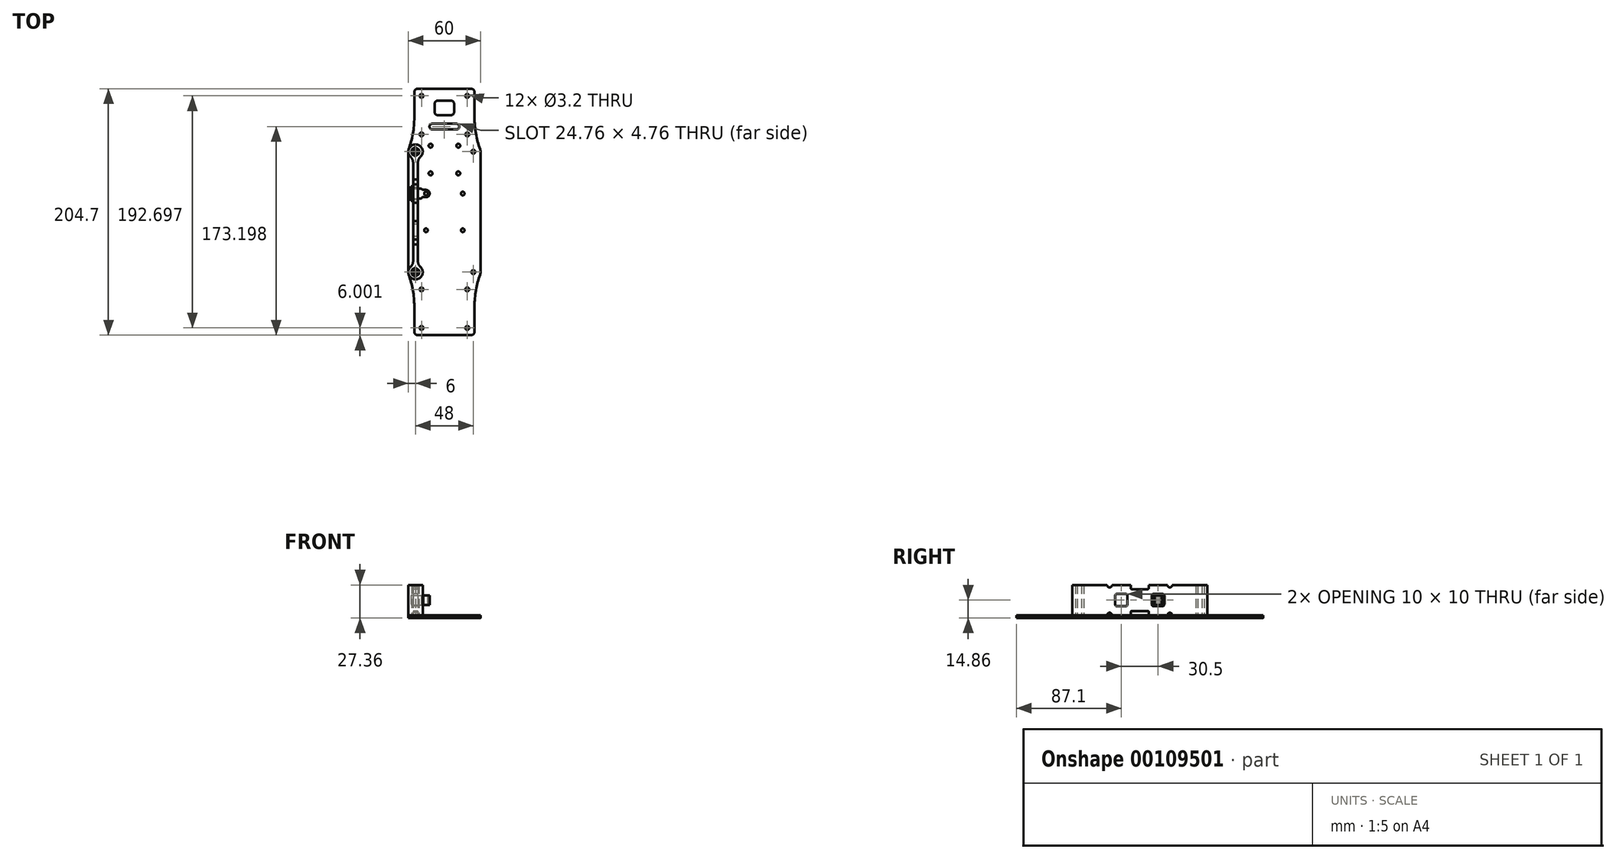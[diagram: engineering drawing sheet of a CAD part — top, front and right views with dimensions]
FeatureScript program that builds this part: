
annotation { "Feature Type Name" : "Feature", "Feature Type Description" : "" }
export const myFeature = defineFeature(function(context is Context, id is Id, definition is map)
    precondition{}
    {
        {
            var Q0;
            Q0=qCreatedBy(makeId("Top.planeOp"),FACE);
            var sketch = newSketch(context, id + "F0", { "sketchPlane" : qUnion([Q0])});
            skLineSegment(sketch, "E0", {"start": v(0, 102.35) * mm, "end": v(-22, 102.35) * mm});
            skLineSegment(sketch, "E1", {"start": v(-25, 99.35) * mm, "end": v(-25, 78.35) * mm});
            skLineSegment(sketch, "E2", {"start": v(-22, -102.35) * mm, "end": v(0, -102.35) * mm});
            skArc(sketch, "E3.filletArc", {"start": v(-22, 102.35) * mm, "mid": v(-24.12, 101.47) * mm, "end": v(-25, 99.35) * mm});
            skArc(sketch, "E4.filletArc", {"start": v(-25, -99.35) * mm, "mid": v(-24.12, -101.47) * mm, "end": v(-22, -102.35) * mm});
            skArc(sketch, "E5.filletArc", {"start": v(-29.64, 52.05) * mm, "mid": v(-29.9, 51.04) * mm, "end": v(-30, 50) * mm});
            skArc(sketch, "E6.MirrorCS", {"start": v(-29.64, -52.05) * mm, "mid": v(-29.9, -51.04) * mm, "end": v(-30, -50) * mm});
            skLineSegment(sketch, "E7.trimOffspring", {"start": v(-25, -78.35) * mm, "end": v(-25, -99.35) * mm});
            skArc(sketch, "E8", {"start": v(-25, -78.35) * mm, "mid": v(-26.17, -65) * mm, "end": v(-29.64, -52.05) * mm});
            skArc(sketch, "E9", {"start": v(-29.64, 52.05) * mm, "mid": v(-26.17, 65) * mm, "end": v(-25, 78.35) * mm});
            skCircle(sketch, "E10", {"center": v(0, 0) * mm, "radius": 125 * mm, "construction": true});
            skLineSegment(sketch, "E11", {"start": v(-95.76, 80.35) * mm, "end": v(95.76, -80.35) * mm, "construction": true});
            skLineSegment(sketch, "E12", {"start": v(95.76, 80.35) * mm, "end": v(-95.76, -80.35) * mm, "construction": true});
            skLineSegment(sketch, "E13", {"start": v(0, 125) * mm, "end": v(0, -125) * mm, "construction": true});
            skLineSegment(sketch, "E14", {"start": v(-95.76, 80.35) * mm, "end": v(95.76, 80.35) * mm, "construction": true});
            skLineSegment(sketch, "E15", {"start": v(-95.76, -80.35) * mm, "end": v(95.76, -80.35) * mm, "construction": true});
            skLineSegment(sketch, "E16", {"start": v(-30, 50) * mm, "end": v(-30, -50) * mm});
            skLineSegment(sketch, "E17.MirrorCS", {"start": v(0, 102.35) * mm, "end": v(22, 102.35) * mm});
            skArc(sketch, "E18.MirrorCS", {"start": v(22, 102.35) * mm, "mid": v(24.12, 101.47) * mm, "end": v(25, 99.35) * mm});
            skLineSegment(sketch, "E19.MirrorCS", {"start": v(25, 99.35) * mm, "end": v(25, 78.35) * mm});
            skArc(sketch, "E20.MirrorCS", {"start": v(29.64, 52.05) * mm, "mid": v(26.17, 65) * mm, "end": v(25, 78.35) * mm});
            skArc(sketch, "E21.MirrorCS", {"start": v(29.64, 52.05) * mm, "mid": v(29.9, 51.04) * mm, "end": v(30, 50) * mm});
            skLineSegment(sketch, "E22.MirrorCS", {"start": v(30, 50) * mm, "end": v(30, -50) * mm});
            skArc(sketch, "E23.MirrorCS", {"start": v(29.64, -52.05) * mm, "mid": v(29.9, -51.04) * mm, "end": v(30, -50) * mm});
            skArc(sketch, "E24.MirrorCS", {"start": v(25, -78.35) * mm, "mid": v(26.17, -65) * mm, "end": v(29.64, -52.05) * mm});
            skArc(sketch, "E25.MirrorCS", {"start": v(25, -99.35) * mm, "mid": v(24.12, -101.47) * mm, "end": v(22, -102.35) * mm});
            skLineSegment(sketch, "E26.MirrorCS", {"start": v(22, -102.35) * mm, "end": v(0, -102.35) * mm});
            skLineSegment(sketch, "E27.MirrorCS", {"start": v(25, -78.35) * mm, "end": v(25, -99.35) * mm});
            skSolve(sketch);
        }
        {
            var Q0;
            Q0=qSketchRegion(id+"F0",true);
            extrude(context, id + "F1", {"entities" : qUnion([Q0]), "oppositeDirection" : true, "depth" : 2.36 * mm});
        }
        {
            var Q0;
            Q0=makeQuery(id+"F1.opExtrude","CAP_FACE",FACE,{"disambiguationData":[OSD([sQuery(id+"F0.wireOp",EDGE,"E0"),sQuery(id+"F0.wireOp",EDGE,"E1"),sQuery(id+"F0.wireOp",EDGE,"E2"),sQuery(id+"F0.wireOp",EDGE,"E3.filletArc"),sQuery(id+"F0.wireOp",EDGE,"E4.filletArc"),sQuery(id+"F0.wireOp",EDGE,"d22b67ea-32aa-4b1a-bfbd-94ae52c1f5b30.MirrorCS"),sQuery(id+"F0.wireOp",EDGE,"d22b67ea-32aa-4b1a-bfbd-94ae52c1f5b31.MirrorCS"),sQuery(id+"F0.wireOp",EDGE,"d22b67ea-32aa-4b1a-bfbd-94ae52c1f5b32.MirrorCS"),sQuery(id+"F0.wireOp",EDGE,"d22b67ea-32aa-4b1a-bfbd-94ae52c1f5b33.MirrorCS"),sQuery(id+"F0.wireOp",EDGE,"d22b67ea-32aa-4b1a-bfbd-94ae52c1f5b34.MirrorCS")])],"isStart":true});
            var sketch = newSketch(context, id + "F2", { "sketchPlane" : qUnion([Q0])});
            skCircle(sketch, "E28", {"center": v(-19, 96.35) * mm, "radius": 1.6 * mm});
            skCircle(sketch, "E29", {"center": v(-19, 64.35) * mm, "radius": 1.6 * mm});
            skCircle(sketch, "E30", {"center": v(-19, -96.35) * mm, "radius": 1.6 * mm});
            skCircle(sketch, "E31", {"center": v(-19, -64.35) * mm, "radius": 1.6 * mm});
            skCircle(sketch, "E32", {"center": v(-24, -50) * mm, "radius": 1.6 * mm});
            skCircle(sketch, "E33", {"center": v(-24, 50) * mm, "radius": 1.6 * mm});
            skLineSegment(sketch, "E34", {"start": v(-19, 96.35) * mm, "end": v(-19, -96.35) * mm, "construction": true});
            skCircle(sketch, "E35.MirrorC", {"center": v(19, 96.35) * mm, "radius": 1.6 * mm});
            skCircle(sketch, "E36.MirrorC", {"center": v(19, 64.35) * mm, "radius": 1.6 * mm});
            skCircle(sketch, "E37.MirrorC", {"center": v(24, 50) * mm, "radius": 1.6 * mm});
            skCircle(sketch, "E38.MirrorC", {"center": v(24, -50) * mm, "radius": 1.6 * mm});
            skCircle(sketch, "E39.MirrorC", {"center": v(19, -64.35) * mm, "radius": 1.6 * mm});
            skCircle(sketch, "E40.MirrorC", {"center": v(19, -96.35) * mm, "radius": 1.6 * mm});
            skLineSegment(sketch, "E41", {"start": v(-15.25, 15.25) * mm, "end": v(-15.25, -15.25) * mm, "construction": true});
            skPoint(sketch, "E42", {"position": v(-15.25, 0) * mm});
            skLineSegment(sketch, "E43", {"start": v(0, 0) * mm, "end": v(-30, 0) * mm, "construction": true});
            skCircle(sketch, "E44", {"center": v(-15.25, -15.25) * mm, "radius": 1.5 * mm});
            skCircle(sketch, "E45", {"center": v(-15.25, 15.25) * mm, "radius": 1.5 * mm});
            skCircle(sketch, "E46.MirrorC", {"center": v(15.25, 15.25) * mm, "radius": 1.5 * mm});
            skCircle(sketch, "E47.MirrorC", {"center": v(15.25, -15.25) * mm, "radius": 1.5 * mm});
            skSolve(sketch);
        }
        {
            var Q0;
            Q0=qSketchRegion(id+"F2",true);
            extrude(context, id + "F3", {"entities" : qUnion([Q0]), "operationType" : NewBodyOperationType.REMOVE, "endBound" : BoundingType.THROUGH_ALL, "oppositeDirection" : true, "depth" : 25.4 * mm});
        }
        {
            var Q0;
            Q0=qCreatedBy(makeId("Top.planeOp"),FACE);
            var sketch = newSketch(context, id + "F4", { "sketchPlane" : qUnion([Q0])});
            skCircle(sketch, "E48.cCircle", {"center": v(-24, 50) * mm, "radius": 3.1 * mm, "construction": true});
            skLineSegment(sketch, "E48.0", {"start": v(-24, 53.58) * mm, "end": v(-20.9, 51.79) * mm, "construction": true});
            skLineSegment(sketch, "E48.1", {"start": v(-20.9, 51.79) * mm, "end": v(-20.9, 48.21) * mm, "construction": true});
            skLineSegment(sketch, "E48.2", {"start": v(-20.9, 48.21) * mm, "end": v(-24, 46.42) * mm, "construction": true});
            skLineSegment(sketch, "E48.3", {"start": v(-24, 46.42) * mm, "end": v(-27.1, 48.21) * mm, "construction": true});
            skLineSegment(sketch, "E48.4", {"start": v(-27.1, 48.21) * mm, "end": v(-27.1, 51.79) * mm, "construction": true});
            skLineSegment(sketch, "E48.5", {"start": v(-27.1, 51.79) * mm, "end": v(-24, 53.58) * mm, "construction": true});
            skPoint(sketch, "E48.0.midPoint", {"position": v(-22.45, 52.68) * mm});
            skArc(sketch, "E49", {"start": v(-20, 45.53) * mm, "mid": v(-24, 56) * mm, "end": v(-28, 45.53) * mm});
            skArc(sketch, "E50", {"start": v(-28, -45.53) * mm, "mid": v(-24, -56) * mm, "end": v(-20, -45.53) * mm});
            skLineSegment(sketch, "E51", {"start": v(-26, 41.06) * mm, "end": v(-26, -41.06) * mm});
            skLineSegment(sketch, "E52", {"start": v(-22, 41.06) * mm, "end": v(-22, -41.06) * mm});
            skPoint(sketch, "E53.visualSharp", {"position": v(-26, 44.34) * mm});
            skArc(sketch, "E53.filletArc", {"start": v(-26, 41.06) * mm, "mid": v(-26.52, 43.5) * mm, "end": v(-28, 45.53) * mm});
            skPoint(sketch, "E54.visualSharp", {"position": v(-22, 44.34) * mm});
            skArc(sketch, "E54.filletArc", {"start": v(-20, 45.53) * mm, "mid": v(-21.48, 43.5) * mm, "end": v(-22, 41.06) * mm});
            skPoint(sketch, "E55.visualSharp", {"position": v(-22, -44.34) * mm});
            skArc(sketch, "E55.filletArc", {"start": v(-22, -41.06) * mm, "mid": v(-21.48, -43.5) * mm, "end": v(-20, -45.53) * mm});
            skPoint(sketch, "E56.visualSharp", {"position": v(-26, -44.34) * mm});
            skArc(sketch, "E56.filletArc", {"start": v(-28, -45.53) * mm, "mid": v(-26.52, -43.5) * mm, "end": v(-26, -41.06) * mm});
            skLineSegment(sketch, "E57", {"start": v(-24, 50) * mm, "end": v(-24, -50) * mm, "construction": true});
            skSolve(sketch);
        }
        {
            var Q0;
            Q0=qSketchRegion(id+"F4",true);
            extrude(context, id + "F5", {"entities" : qUnion([Q0]), "depth" : 25 * mm});
        }
        {
            var Q0;
            Q0=makeQuery(id+"F5.opExtrude","CAP_FACE",FACE,{"disambiguationData":[OSD([sQuery(id+"F4.wireOp",EDGE,"E49"),sQuery(id+"F4.wireOp",EDGE,"E50"),sQuery(id+"F4.wireOp",EDGE,"E51"),sQuery(id+"F4.wireOp",EDGE,"E52"),sQuery(id+"F4.wireOp",EDGE,"E53.filletArc"),sQuery(id+"F4.wireOp",EDGE,"E54.filletArc"),sQuery(id+"F4.wireOp",EDGE,"E55.filletArc"),sQuery(id+"F4.wireOp",EDGE,"E56.filletArc")])],"isStart":true});
            var sketch = newSketch(context, id + "F6", { "sketchPlane" : qUnion([Q0])});
            skCircle(sketch, "E58.cCircle", {"center": v(-24, -50) * mm, "radius": 3.05 * mm, "construction": true});
            skLineSegment(sketch, "E58.0", {"start": v(-27.05, -48.24) * mm, "end": v(-24, -46.48) * mm});
            skLineSegment(sketch, "E58.1", {"start": v(-24, -46.48) * mm, "end": v(-20.95, -48.24) * mm});
            skLineSegment(sketch, "E58.2", {"start": v(-20.95, -48.24) * mm, "end": v(-20.95, -51.76) * mm});
            skLineSegment(sketch, "E58.3", {"start": v(-20.95, -51.76) * mm, "end": v(-24, -53.52) * mm});
            skLineSegment(sketch, "E58.4", {"start": v(-24, -53.52) * mm, "end": v(-27.05, -51.76) * mm});
            skLineSegment(sketch, "E58.5", {"start": v(-27.05, -51.76) * mm, "end": v(-27.05, -48.24) * mm});
            skPoint(sketch, "E58.0.midPoint", {"position": v(-25.53, -47.36) * mm});
            skCircle(sketch, "E59.cCircle", {"center": v(-24, 50) * mm, "radius": 3.05 * mm, "construction": true});
            skLineSegment(sketch, "E59.0", {"start": v(-27.05, 51.76) * mm, "end": v(-24, 53.52) * mm});
            skLineSegment(sketch, "E59.1", {"start": v(-24, 53.52) * mm, "end": v(-20.95, 51.76) * mm});
            skLineSegment(sketch, "E59.2", {"start": v(-20.95, 51.76) * mm, "end": v(-20.95, 48.24) * mm});
            skLineSegment(sketch, "E59.3", {"start": v(-20.95, 48.24) * mm, "end": v(-24, 46.48) * mm});
            skLineSegment(sketch, "E59.4", {"start": v(-24, 46.48) * mm, "end": v(-27.05, 48.24) * mm});
            skLineSegment(sketch, "E59.5", {"start": v(-27.05, 48.24) * mm, "end": v(-27.05, 51.76) * mm});
            skPoint(sketch, "E59.0.midPoint", {"position": v(-25.52, 52.64) * mm});
            skSolve(sketch);
        }
        {
            var Q0;
            Q0=qSketchRegion(id+"F6",true);
            var Q1;
            Q1=makeQuery(id+"F5.opExtrude","CAP_FACE",FACE,{"disambiguationData":[OSD([sQuery(id+"F4.wireOp",EDGE,"E49"),sQuery(id+"F4.wireOp",EDGE,"E50"),sQuery(id+"F4.wireOp",EDGE,"E51"),sQuery(id+"F4.wireOp",EDGE,"E52"),sQuery(id+"F4.wireOp",EDGE,"E53.filletArc"),sQuery(id+"F4.wireOp",EDGE,"E54.filletArc"),sQuery(id+"F4.wireOp",EDGE,"E55.filletArc"),sQuery(id+"F4.wireOp",EDGE,"E56.filletArc")])],"isStart":false});
            extrude(context, id + "F7", {"entities" : qUnion([Q0]), "operationType" : NewBodyOperationType.REMOVE, "endBound" : BoundingType.UP_TO_SURFACE, "oppositeDirection" : true, "endBoundEntityFace" : qUnion([Q1]), "depth" : 25 * mm});
        }
        {
            var Q0;
            Q0=makeQuery(id+"F5.opExtrude","SWEPT_FACE",FACE,{"disambiguationData":[OSD([sQuery(id+"F4.wireOp",EDGE,"E51")])]});
            var sketch = newSketch(context, id + "F8", { "sketchPlane" : qUnion([Q0])});
            skLineSegment(sketch, "E60", {"start": v(-21.13, 12.5) * mm, "end": v(21.13, 12.5) * mm, "construction": true});
            skLineSegment(sketch, "E61.bottom", {"start": v(-11.25, 17.5) * mm, "end": v(-19.25, 17.5) * mm});
            skLineSegment(sketch, "E61.top", {"start": v(-11.25, 7.5) * mm, "end": v(-19.25, 7.5) * mm});
            skLineSegment(sketch, "E61.left", {"start": v(-10.25, 16.5) * mm, "end": v(-10.25, 8.5) * mm});
            skLineSegment(sketch, "E61.right", {"start": v(-20.25, 16.5) * mm, "end": v(-20.25, 8.5) * mm});
            skPoint(sketch, "E61.middle", {"position": v(-15.25, 12.5) * mm});
            skPoint(sketch, "E62.visualSharp", {"position": v(-20.25, 17.5) * mm});
            skArc(sketch, "E62.filletArc", {"start": v(-19.25, 17.5) * mm, "mid": v(-19.96, 17.2) * mm, "end": v(-20.25, 16.5) * mm});
            skPoint(sketch, "E63.visualSharp", {"position": v(-20.25, 7.5) * mm});
            skArc(sketch, "E63.filletArc", {"start": v(-20.25, 8.5) * mm, "mid": v(-19.96, 7.8) * mm, "end": v(-19.25, 7.5) * mm});
            skPoint(sketch, "E64.visualSharp", {"position": v(-10.25, 7.5) * mm});
            skArc(sketch, "E64.filletArc", {"start": v(-11.25, 7.5) * mm, "mid": v(-10.54, 7.8) * mm, "end": v(-10.25, 8.5) * mm});
            skPoint(sketch, "E65.visualSharp", {"position": v(-10.25, 17.5) * mm});
            skArc(sketch, "E65.filletArc", {"start": v(-10.25, 16.5) * mm, "mid": v(-10.54, 17.2) * mm, "end": v(-11.25, 17.5) * mm});
            skLineSegment(sketch, "E66.bottom", {"start": v(-7.5, 0) * mm, "end": v(7.5, 0) * mm});
            skLineSegment(sketch, "E66.top", {"start": v(-6.5, 3.5) * mm, "end": v(6.5, 3.5) * mm});
            skLineSegment(sketch, "E66.left", {"start": v(-7.5, 0) * mm, "end": v(-7.5, 2.5) * mm});
            skLineSegment(sketch, "E66.right", {"start": v(7.5, 0) * mm, "end": v(7.5, 2.5) * mm});
            skPoint(sketch, "E67.visualSharp", {"position": v(-7.5, 3.5) * mm});
            skArc(sketch, "E67.filletArc", {"start": v(-6.5, 3.5) * mm, "mid": v(-7.2, 3.2) * mm, "end": v(-7.5, 2.5) * mm});
            skPoint(sketch, "E68.visualSharp", {"position": v(7.5, 3.5) * mm});
            skArc(sketch, "E68.filletArc", {"start": v(7.5, 2.5) * mm, "mid": v(7.2, 3.2) * mm, "end": v(6.5, 3.5) * mm});
            skArc(sketch, "E69", {"start": v(-27, 25) * mm, "mid": v(-25, 23) * mm, "end": v(-23, 25) * mm});
            skLineSegment(sketch, "E70", {"start": v(-25, 25) * mm, "end": v(-25, 0) * mm, "construction": true});
            skArc(sketch, "E71", {"start": v(-23, 0) * mm, "mid": v(-25, 2) * mm, "end": v(-27, 0) * mm});
            skLineSegment(sketch, "E72", {"start": v(-27, 25) * mm, "end": v(-23, 25) * mm});
            skLineSegment(sketch, "E73", {"start": v(-27, 0) * mm, "end": v(-23, 0) * mm});
            skLineSegment(sketch, "E74", {"start": v(0, 25) * mm, "end": v(0, 0) * mm, "construction": true});
            skPoint(sketch, "E75", {"position": v(0, 12.5) * mm});
            skArc(sketch, "E76.MirrorCS", {"start": v(11.25, 7.5) * mm, "mid": v(10.54, 7.8) * mm, "end": v(10.25, 8.5) * mm});
            skArc(sketch, "E77.MirrorCS", {"start": v(10.25, 16.5) * mm, "mid": v(10.54, 17.2) * mm, "end": v(11.25, 17.5) * mm});
            skArc(sketch, "E78.MirrorCS", {"start": v(20.25, 8.5) * mm, "mid": v(19.96, 7.8) * mm, "end": v(19.25, 7.5) * mm});
            skArc(sketch, "E79.MirrorCS", {"start": v(19.25, 17.5) * mm, "mid": v(19.96, 17.2) * mm, "end": v(20.25, 16.5) * mm});
            skPoint(sketch, "E80.MirrorP", {"position": v(10.25, 17.5) * mm});
            skLineSegment(sketch, "E81.MirrorCS", {"start": v(20.25, 16.5) * mm, "end": v(20.25, 8.5) * mm});
            skLineSegment(sketch, "E82.MirrorCS", {"start": v(10.25, 16.5) * mm, "end": v(10.25, 8.5) * mm});
            skLineSegment(sketch, "E83.MirrorCS", {"start": v(11.25, 17.5) * mm, "end": v(19.25, 17.5) * mm});
            skLineSegment(sketch, "E84.MirrorCS", {"start": v(11.25, 7.5) * mm, "end": v(19.25, 7.5) * mm});
            skPoint(sketch, "E85.MirrorP", {"position": v(20.25, 7.5) * mm});
            skPoint(sketch, "E86.MirrorP", {"position": v(15.25, 12.5) * mm});
            skPoint(sketch, "E87.MirrorP", {"position": v(20.25, 17.5) * mm});
            skPoint(sketch, "E88.MirrorP", {"position": v(10.25, 7.5) * mm});
            skLineSegment(sketch, "E89.MirrorCS", {"start": v(27, 25) * mm, "end": v(23, 25) * mm});
            skLineSegment(sketch, "E90.MirrorCS", {"start": v(25, 25) * mm, "end": v(25, 0) * mm, "construction": true});
            skArc(sketch, "E91.MirrorCS", {"start": v(27, 25) * mm, "mid": v(25, 23) * mm, "end": v(23, 25) * mm});
            skLineSegment(sketch, "E92.MirrorCS", {"start": v(27, 0) * mm, "end": v(23, 0) * mm});
            skArc(sketch, "E93.MirrorCS", {"start": v(23, 0) * mm, "mid": v(25, 2) * mm, "end": v(27, 0) * mm});
            skArc(sketch, "E94.MirrorCS", {"start": v(-6.5, 21.5) * mm, "mid": v(-7.2, 21.8) * mm, "end": v(-7.5, 22.5) * mm});
            skArc(sketch, "E95.MirrorCS", {"start": v(7.5, 22.5) * mm, "mid": v(7.2, 21.8) * mm, "end": v(6.5, 21.5) * mm});
            skPoint(sketch, "E96.MirrorP", {"position": v(-7.5, 21.5) * mm});
            skLineSegment(sketch, "E97.MirrorCS", {"start": v(-6.5, 21.5) * mm, "end": v(6.5, 21.5) * mm});
            skLineSegment(sketch, "E98.MirrorCS", {"start": v(-7.5, 25) * mm, "end": v(-7.5, 22.5) * mm});
            skPoint(sketch, "E99.MirrorP", {"position": v(7.5, 21.5) * mm});
            skLineSegment(sketch, "E100.MirrorCS", {"start": v(7.5, 25) * mm, "end": v(7.5, 22.5) * mm});
            skLineSegment(sketch, "E101.MirrorCS", {"start": v(-7.5, 25) * mm, "end": v(7.5, 25) * mm});
            skSolve(sketch);
        }
        {
            var Q0;
            Q0=qSketchRegion(id+"F8",true);
            var Q1;
            Q1=makeQuery(id+"F5.opExtrude","SWEPT_FACE",FACE,{"disambiguationData":[OSD([sQuery(id+"F4.wireOp",EDGE,"E52")])]});
            extrude(context, id + "F9", {"entities" : qUnion([Q0]), "operationType" : NewBodyOperationType.REMOVE, "endBound" : BoundingType.UP_TO_SURFACE, "oppositeDirection" : true, "endBoundEntityFace" : qUnion([Q1]), "depth" : 25 * mm});
        }
        {
            var Q0;
            Q0=qCreatedBy(makeId("Top.planeOp"),FACE);
            cPlane(context, id + "F10", {"entities" : qUnion([Q0]), "cplaneType" : CPlaneType.OFFSET, "offset" : 12.5 * mm, "width" : 150 * mm, "height" : 150 * mm});
        }
        {
            var Q0;
            Q0=qCreatedBy(id+"F10.planeOp",FACE);
            var sketch = newSketch(context, id + "F11", { "sketchPlane" : qUnion([Q0])});
            skLineSegment(sketch, "E102", {"start": v(-26.25, 21.25) * mm, "end": v(-26.25, 19.75) * mm});
            skLineSegment(sketch, "E103", {"start": v(-25.75, 19.25) * mm, "end": v(-19.25, 19.25) * mm});
            skLineSegment(sketch, "E104", {"start": v(-19.25, 19.25) * mm, "end": v(-18.25, 18.25) * mm});
            skLineSegment(sketch, "E105", {"start": v(-18.25, 18.25) * mm, "end": v(-15.25, 18.25) * mm});
            skLineSegment(sketch, "E106", {"start": v(-6.48, 15.25) * mm, "end": v(-35.06, 15.25) * mm, "construction": true});
            skArc(sketch, "E107", {"start": v(-12.25, 15.25) * mm, "mid": v(-13.13, 17.37) * mm, "end": v(-15.25, 18.25) * mm});
            skLineSegment(sketch, "E108", {"start": v(-26.25, 21.25) * mm, "end": v(-27.75, 21.25) * mm});
            skLineSegment(sketch, "E109", {"start": v(-27.75, 21.25) * mm, "end": v(-27.75, 15.25) * mm});
            skPoint(sketch, "E110.visualSharp", {"position": v(-26.25, 19.25) * mm});
            skArc(sketch, "E110.filletArc", {"start": v(-26.25, 19.75) * mm, "mid": v(-26.1, 19.4) * mm, "end": v(-25.75, 19.25) * mm});
            skLineSegment(sketch, "E111.MirrorCS", {"start": v(-27.75, 9.25) * mm, "end": v(-27.75, 15.25) * mm});
            skLineSegment(sketch, "E112.MirrorCS", {"start": v(-26.25, 9.25) * mm, "end": v(-27.75, 9.25) * mm});
            skLineSegment(sketch, "E113.MirrorCS", {"start": v(-26.25, 9.25) * mm, "end": v(-26.25, 10.75) * mm});
            skArc(sketch, "E114.MirrorCS", {"start": v(-26.25, 10.75) * mm, "mid": v(-26.1, 11.1) * mm, "end": v(-25.75, 11.25) * mm});
            skLineSegment(sketch, "E115.MirrorCS", {"start": v(-25.75, 11.25) * mm, "end": v(-19.25, 11.25) * mm});
            skLineSegment(sketch, "E116.MirrorCS", {"start": v(-19.25, 11.25) * mm, "end": v(-18.25, 12.25) * mm});
            skLineSegment(sketch, "E117.MirrorCS", {"start": v(-18.25, 12.25) * mm, "end": v(-15.25, 12.25) * mm});
            skArc(sketch, "E118.MirrorCS", {"start": v(-12.25, 15.25) * mm, "mid": v(-13.13, 13.13) * mm, "end": v(-15.25, 12.25) * mm});
            skSolve(sketch);
        }
        {
            var Q0;
            Q0=qSketchRegion(id+"F11",true);
            extrude(context, id + "F12", {"entities" : qUnion([Q0]), "endBound" : BoundingType.SYMMETRIC, "depth" : 8 * mm});
        }
        {
            var Q0;
            Q0=makeQuery(id+"F12.opExtrude","CAP_FACE",FACE,{"disambiguationData":[OSD([sQuery(id+"F11.wireOp",EDGE,"E102"),sQuery(id+"F11.wireOp",EDGE,"E103"),sQuery(id+"F11.wireOp",EDGE,"E104"),sQuery(id+"F11.wireOp",EDGE,"E105"),sQuery(id+"F11.wireOp",EDGE,"E107"),sQuery(id+"F11.wireOp",EDGE,"E108"),sQuery(id+"F11.wireOp",EDGE,"E109"),sQuery(id+"F11.wireOp",EDGE,"E110.filletArc"),sQuery(id+"F11.wireOp",EDGE,"E111.MirrorCS"),sQuery(id+"F11.wireOp",EDGE,"E112.MirrorCS"),sQuery(id+"F11.wireOp",EDGE,"E113.MirrorCS"),sQuery(id+"F11.wireOp",EDGE,"E114.MirrorCS"),sQuery(id+"F11.wireOp",EDGE,"E115.MirrorCS"),sQuery(id+"F11.wireOp",EDGE,"E116.MirrorCS"),sQuery(id+"F11.wireOp",EDGE,"E117.MirrorCS"),sQuery(id+"F11.wireOp",EDGE,"E118.MirrorCS")])],"isStart":false});
            var sketch = newSketch(context, id + "F13", { "sketchPlane" : qUnion([Q0])});
            skCircle(sketch, "E119", {"center": v(-15.25, 15.25) * mm, "radius": 1.5 * mm});
            skSolve(sketch);
        }
        {
            var Q0;
            Q0=qSketchRegion(id+"F13",true);
            var Q1;
            Q1=makeQuery(id+"F12.opExtrude","CAP_FACE",FACE,{"disambiguationData":[OSD([sQuery(id+"F11.wireOp",EDGE,"E102"),sQuery(id+"F11.wireOp",EDGE,"E103"),sQuery(id+"F11.wireOp",EDGE,"E104"),sQuery(id+"F11.wireOp",EDGE,"E105"),sQuery(id+"F11.wireOp",EDGE,"E107"),sQuery(id+"F11.wireOp",EDGE,"E108"),sQuery(id+"F11.wireOp",EDGE,"E109"),sQuery(id+"F11.wireOp",EDGE,"E110.filletArc"),sQuery(id+"F11.wireOp",EDGE,"E111.MirrorCS"),sQuery(id+"F11.wireOp",EDGE,"E112.MirrorCS"),sQuery(id+"F11.wireOp",EDGE,"E113.MirrorCS"),sQuery(id+"F11.wireOp",EDGE,"E114.MirrorCS"),sQuery(id+"F11.wireOp",EDGE,"E115.MirrorCS"),sQuery(id+"F11.wireOp",EDGE,"E116.MirrorCS"),sQuery(id+"F11.wireOp",EDGE,"E117.MirrorCS"),sQuery(id+"F11.wireOp",EDGE,"E118.MirrorCS")])],"isStart":true});
            extrude(context, id + "F14", {"entities" : qUnion([Q0]), "operationType" : NewBodyOperationType.REMOVE, "endBound" : BoundingType.UP_TO_SURFACE, "oppositeDirection" : true, "endBoundEntityFace" : qUnion([Q1]), "depth" : 25 * mm});
        }
        {
            var Q0;
            Q0=qCreatedBy(makeId("Top.planeOp"),FACE);
            var sketch = newSketch(context, id + "F15", { "sketchPlane" : qUnion([Q0])});
            skLineSegment(sketch, "E120.bottom", {"start": v(-10, 73.23) * mm, "end": v(10, 73.23) * mm});
            skLineSegment(sketch, "E120.top", {"start": v(-10, 68.47) * mm, "end": v(10, 68.47) * mm});
            skPoint(sketch, "E121", {"position": v(0, 73.23) * mm});
            skArc(sketch, "E122", {"start": v(-10, 73.23) * mm, "mid": v(-12.38, 70.85) * mm, "end": v(-10, 68.47) * mm});
            skArc(sketch, "E123", {"start": v(10, 68.47) * mm, "mid": v(12.38, 70.85) * mm, "end": v(10, 73.23) * mm});
            skLineSegment(sketch, "E124.bottom", {"start": v(-5.62, 92.35) * mm, "end": v(5.62, 92.35) * mm});
            skLineSegment(sketch, "E124.top", {"start": v(-5.62, 80.35) * mm, "end": v(5.62, 80.35) * mm});
            skLineSegment(sketch, "E124.left", {"start": v(-8, 89.97) * mm, "end": v(-8, 82.73) * mm});
            skLineSegment(sketch, "E124.right", {"start": v(8, 89.97) * mm, "end": v(8, 82.73) * mm});
            skPoint(sketch, "E125", {"position": v(0, 92.35) * mm});
            skPoint(sketch, "E126.visualSharp", {"position": v(-8, 92.35) * mm});
            skArc(sketch, "E126.filletArc", {"start": v(-5.62, 92.35) * mm, "mid": v(-7.3, 91.65) * mm, "end": v(-8, 89.97) * mm});
            skPoint(sketch, "E127.visualSharp", {"position": v(-8, 80.35) * mm});
            skArc(sketch, "E127.filletArc", {"start": v(-8, 82.73) * mm, "mid": v(-7.3, 81.05) * mm, "end": v(-5.62, 80.35) * mm});
            skPoint(sketch, "E128.visualSharp", {"position": v(8, 80.35) * mm});
            skArc(sketch, "E128.filletArc", {"start": v(5.62, 80.35) * mm, "mid": v(7.3, 81.05) * mm, "end": v(8, 82.73) * mm});
            skPoint(sketch, "E129.visualSharp", {"position": v(8, 92.35) * mm});
            skArc(sketch, "E129.filletArc", {"start": v(8, 89.97) * mm, "mid": v(7.3, 91.65) * mm, "end": v(5.62, 92.35) * mm});
            skLineSegment(sketch, "E130.bottom", {"start": v(-11.5, 55) * mm, "end": v(11.5, 55) * mm, "construction": true});
            skLineSegment(sketch, "E130.top", {"start": v(-11.5, 32) * mm, "end": v(11.5, 32) * mm, "construction": true});
            skLineSegment(sketch, "E130.left", {"start": v(-11.5, 55) * mm, "end": v(-11.5, 32) * mm, "construction": true});
            skLineSegment(sketch, "E130.right", {"start": v(11.5, 55) * mm, "end": v(11.5, 32) * mm, "construction": true});
            skPoint(sketch, "E131", {"position": v(0, 55) * mm});
            skCircle(sketch, "E132", {"center": v(-11.5, 55) * mm, "radius": 1.59 * mm});
            skCircle(sketch, "E133", {"center": v(11.5, 55) * mm, "radius": 1.59 * mm});
            skCircle(sketch, "E134", {"center": v(-11.5, 32) * mm, "radius": 1.59 * mm});
            skCircle(sketch, "E135", {"center": v(11.5, 32) * mm, "radius": 1.59 * mm});
            skSolve(sketch);
        }
        {
            var Q0;
            Q0=qSketchRegion(id+"F15",true);
            var Q1;
            Q1=makeQuery(id+"F1.opExtrude","CAP_FACE",FACE,{"disambiguationData":[OSD([sQuery(id+"F0.wireOp",EDGE,"E0"),sQuery(id+"F0.wireOp",EDGE,"E1"),sQuery(id+"F0.wireOp",EDGE,"E2"),sQuery(id+"F0.wireOp",EDGE,"E3.filletArc"),sQuery(id+"F0.wireOp",EDGE,"E4.filletArc"),sQuery(id+"F0.wireOp",EDGE,"E5.filletArc"),sQuery(id+"F0.wireOp",EDGE,"E6.MirrorCS"),sQuery(id+"F0.wireOp",EDGE,"E7.trimOffspring"),sQuery(id+"F0.wireOp",EDGE,"E8"),sQuery(id+"F0.wireOp",EDGE,"E9"),sQuery(id+"F0.wireOp",EDGE,"E16"),sQuery(id+"F0.wireOp",EDGE,"E17.MirrorCS"),sQuery(id+"F0.wireOp",EDGE,"E18.MirrorCS"),sQuery(id+"F0.wireOp",EDGE,"E19.MirrorCS"),sQuery(id+"F0.wireOp",EDGE,"E20.MirrorCS"),sQuery(id+"F0.wireOp",EDGE,"E21.MirrorCS"),sQuery(id+"F0.wireOp",EDGE,"E22.MirrorCS"),sQuery(id+"F0.wireOp",EDGE,"E23.MirrorCS"),sQuery(id+"F0.wireOp",EDGE,"E24.MirrorCS"),sQuery(id+"F0.wireOp",EDGE,"E25.MirrorCS"),sQuery(id+"F0.wireOp",EDGE,"E26.MirrorCS"),sQuery(id+"F0.wireOp",EDGE,"E27.MirrorCS")])],"isStart":false});
            extrude(context, id + "F16", {"entities" : qUnion([Q0]), "operationType" : NewBodyOperationType.REMOVE, "endBound" : BoundingType.UP_TO_SURFACE, "oppositeDirection" : true, "endBoundEntityFace" : qUnion([Q1]), "depth" : 25 * mm});
        }
    });
